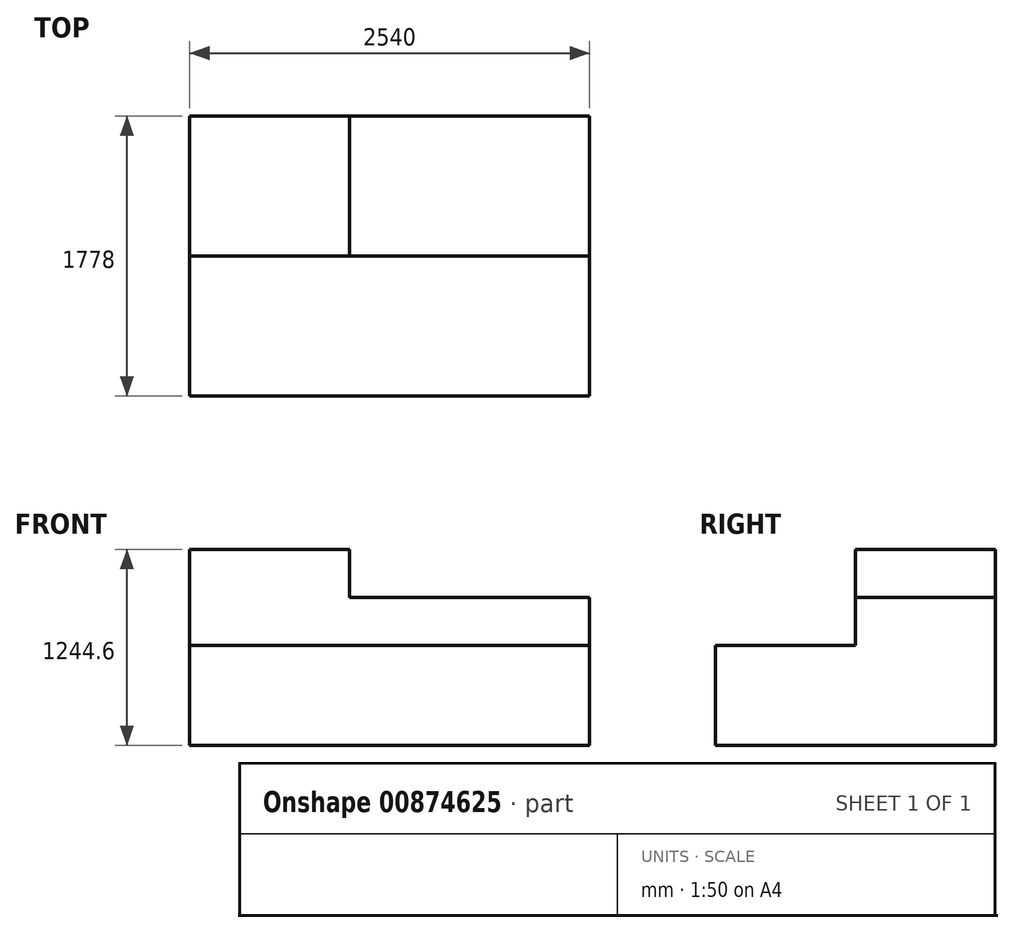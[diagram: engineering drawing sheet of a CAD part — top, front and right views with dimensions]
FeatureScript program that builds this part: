
annotation { "Feature Type Name" : "Feature", "Feature Type Description" : "" }
export const myFeature = defineFeature(function(context is Context, id is Id, definition is map)
    precondition{}
    {
        {
            var Q0;
            Q0=qCreatedBy(makeId("Top.planeOp"),FACE);
            var sketch = newSketch(context, id + "F0", { "sketchPlane" : qUnion([Q0])});
            skLineSegment(sketch, "E0.bottom", {"start": v(0, 0) * mm, "end": v(-2540, 0) * mm});
            skLineSegment(sketch, "E0.top", {"start": v(0, -1778) * mm, "end": v(-2540, -1778) * mm});
            skLineSegment(sketch, "E0.left", {"start": v(0, 0) * mm, "end": v(0, -1778) * mm});
            skLineSegment(sketch, "E0.right", {"start": v(-2540, 0) * mm, "end": v(-2540, -1778) * mm});
            skSolve(sketch);
        }
        {
            var Q0;
            Q0=qSketchRegion(id+"F0",true);
            extrude(context, id + "F1", {"entities" : qUnion([Q0]), "depth" : 635 * mm, "offsetDistance" : 25.4 * mm});
        }
        {
            var Q0;
            Q0=makeQuery(id+"F1.opExtrude","CAP_FACE",FACE,{"disambiguationData":[OSD([sQuery(id+"F0.wireOp",EDGE,"E0.bottom"),sQuery(id+"F0.wireOp",EDGE,"E0.top"),sQuery(id+"F0.wireOp",EDGE,"E0.left"),sQuery(id+"F0.wireOp",EDGE,"E0.right")])],"isStart":false});
            var sketch = newSketch(context, id + "F2", { "sketchPlane" : qUnion([Q0])});
            skLineSegment(sketch, "E1.bottom", {"start": v(0, 0) * mm, "end": v(-2540, 0) * mm});
            skLineSegment(sketch, "E1.top", {"start": v(0, -889) * mm, "end": v(-2540, -889) * mm});
            skLineSegment(sketch, "E1.left", {"start": v(0, 0) * mm, "end": v(0, -889) * mm});
            skLineSegment(sketch, "E1.right", {"start": v(-2540, 0) * mm, "end": v(-2540, -889) * mm});
            skSolve(sketch);
        }
        {
            var Q0;
            Q0=makeQuery(id+"F2.imprint","IMPRINT",FACE,{"disambiguationData":[TD([[makeQuery(id+"F2.imprint","IMPRINT",EDGE,{"derivedFrom":sQuery(id+"F2.wireOp",EDGE,"E1.bottom")}),1.0]])]});
            extrude(context, id + "F3", {"entities" : qUnion([Q0]), "operationType" : NewBodyOperationType.ADD, "depth" : 304.8 * mm, "offsetDistance" : 25.4 * mm});
        }
        {
            var Q0;
            Q0=makeQuery(id+"F3.opExtrude","CAP_FACE",FACE,{"disambiguationData":[OSD([sQuery(id+"F2.wireOp",EDGE,"E1.bottom"),sQuery(id+"F2.wireOp",EDGE,"E1.top"),sQuery(id+"F2.wireOp",EDGE,"E1.left"),sQuery(id+"F2.wireOp",EDGE,"E1.right")])],"isStart":false});
            var sketch = newSketch(context, id + "F4", { "sketchPlane" : qUnion([Q0])});
            skLineSegment(sketch, "E2.bottom", {"start": v(-2540, 0) * mm, "end": v(-1524, 0) * mm});
            skLineSegment(sketch, "E2.top", {"start": v(-2540, -889) * mm, "end": v(-1524, -889) * mm});
            skLineSegment(sketch, "E2.left", {"start": v(-2540, 0) * mm, "end": v(-2540, -889) * mm});
            skLineSegment(sketch, "E2.right", {"start": v(-1524, 0) * mm, "end": v(-1524, -889) * mm});
            skSolve(sketch);
        }
        {
            var Q0;
            Q0=makeQuery(id+"F4.imprint","IMPRINT",FACE,{"disambiguationData":[TD([[makeQuery(id+"F4.imprint","IMPRINT",EDGE,{"derivedFrom":sQuery(id+"F4.wireOp",EDGE,"E2.bottom")}),1.0]])]});
            extrude(context, id + "F5", {"entities" : qUnion([Q0]), "operationType" : NewBodyOperationType.ADD, "depth" : 304.8 * mm, "offsetDistance" : 25.4 * mm});
        }
    });
